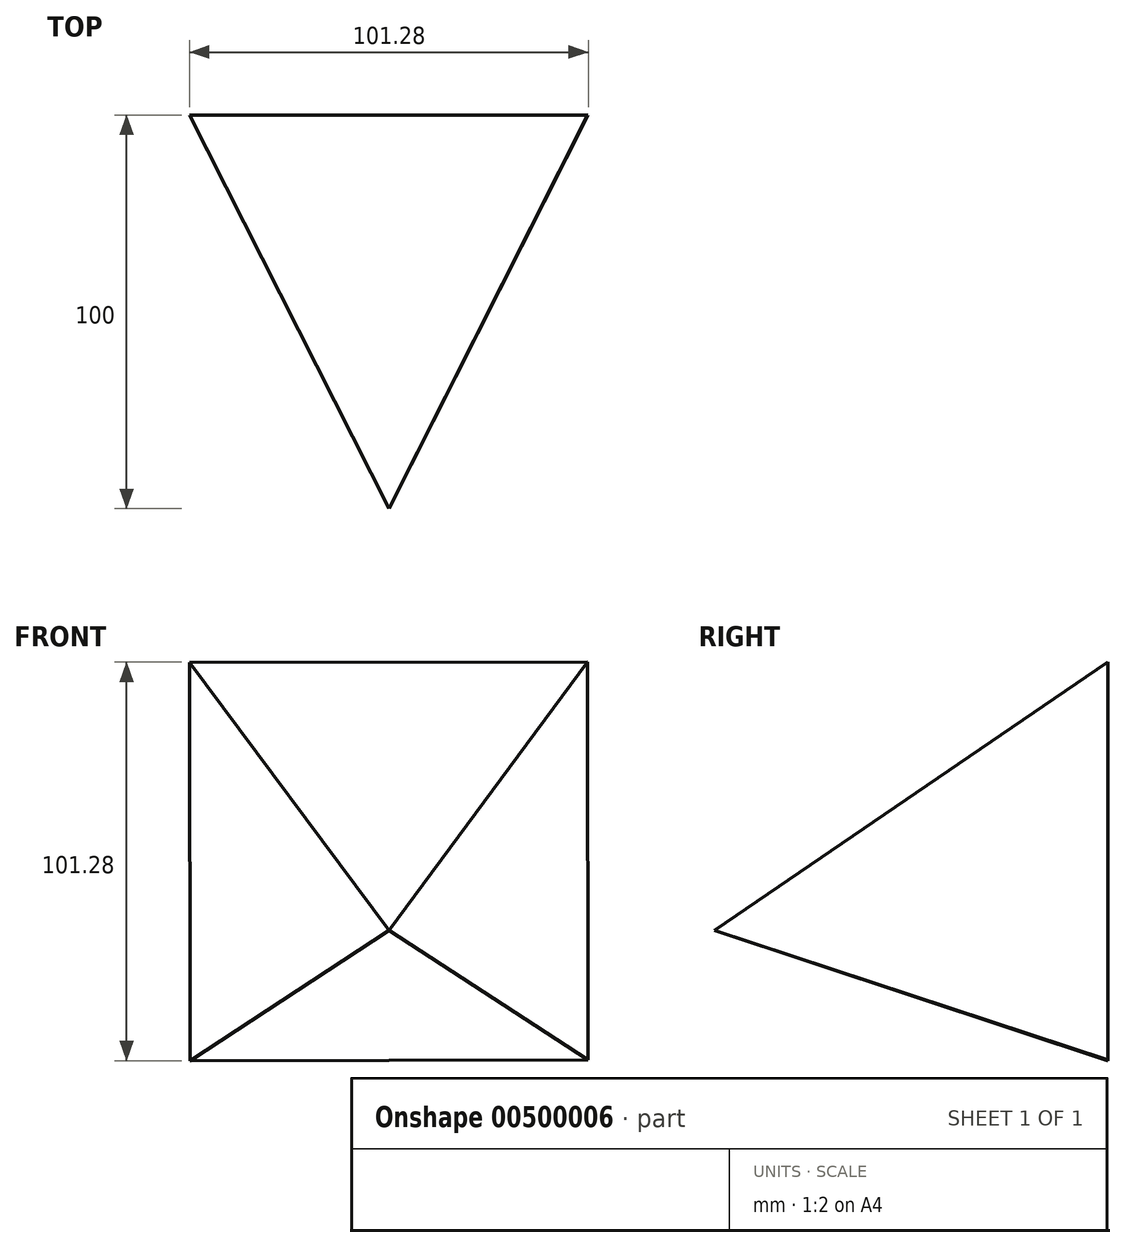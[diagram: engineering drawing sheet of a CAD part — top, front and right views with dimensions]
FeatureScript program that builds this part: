
annotation { "Feature Type Name" : "Feature", "Feature Type Description" : "" }
export const myFeature = defineFeature(function(context is Context, id is Id, definition is map)
    precondition{}
    {
        {
            var Q0;
            Q0=qCreatedBy(makeId("Front.planeOp"),FACE);
            var sketch = newSketch(context, id + "F0", { "sketchPlane" : qUnion([Q0])});
            skCircle(sketch, "E0.cCircle", {"center": v(0, 0) * mm, "radius": 71.5 * mm, "construction": true});
            skLineSegment(sketch, "E0.0", {"start": v(-50.64, 50.5) * mm, "end": v(50.5, 50.64) * mm});
            skLineSegment(sketch, "E0.1", {"start": v(50.5, 50.64) * mm, "end": v(50.64, -50.5) * mm});
            skLineSegment(sketch, "E0.2", {"start": v(50.64, -50.5) * mm, "end": v(-50.5, -50.64) * mm});
            skLineSegment(sketch, "E0.3", {"start": v(-50.5, -50.64) * mm, "end": v(-50.64, 50.5) * mm});
            skSolve(sketch);
        }
        {
            var Q0;
            Q0=qCreatedBy(makeId("Front.planeOp"),FACE);
            cPlane(context, id + "F1", {"entities" : qUnion([Q0]), "cplaneType" : CPlaneType.OFFSET, "offset" : 100 * mm, "width" : 150 * mm, "height" : 150 * mm});
        }
        {
            var Q0;
            Q0=qCreatedBy(id+"F1.planeOp",FACE);
            var sketch = newSketch(context, id + "F2", { "sketchPlane" : qUnion([Q0])});
            skPoint(sketch, "E1", {"position": v(0, -17.53) * mm});
            skSolve(sketch);
        }
        {
            var Q0;
            Q0=makeQuery(id+"F0.imprint","IMPRINT",FACE,{"disambiguationData":[TD([[makeQuery(id+"F0.imprint","IMPRINT",EDGE,{"derivedFrom":sQuery(id+"F0.wireOp",EDGE,"E0.0")}),-1.0]])]});
            var Q1;
            Q1=sQuery(id+"F2.wireOp",VERTEX,"E1");
            loft(context, id + "F3", {"sheetProfilesArray" : [{ "sheetProfileEntities" : qUnion([Q0]) }, { "sheetProfileEntities" : qUnion([Q1]) }]});
        }
    });
